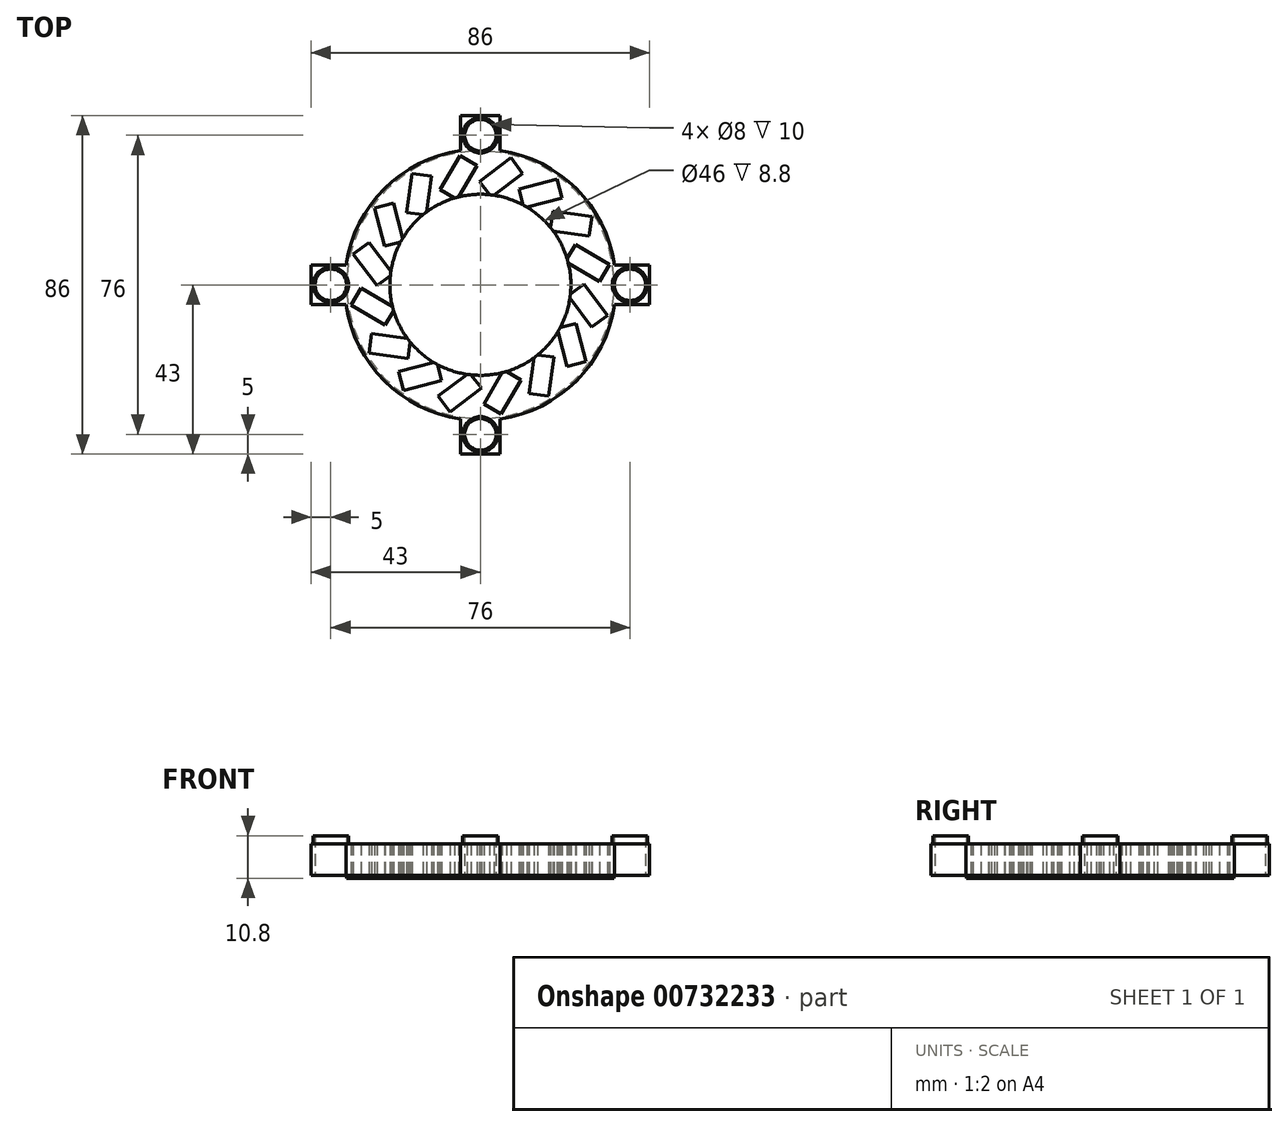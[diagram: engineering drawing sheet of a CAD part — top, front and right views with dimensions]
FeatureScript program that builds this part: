
annotation { "Feature Type Name" : "Feature", "Feature Type Description" : "" }
export const myFeature = defineFeature(function(context is Context, id is Id, definition is map)
    precondition{}
    {
        {
            var Q0;
            Q0=qCreatedBy(makeId("Top.planeOp"),FACE);
            var sketch = newSketch(context, id + "F0", { "sketchPlane" : qUnion([Q0])});
            skCircle(sketch, "E0", {"center": v(0, 0) * mm, "radius": 23 * mm});
            skCircle(sketch, "E1", {"center": v(0, 0) * mm, "radius": 34 * mm});
            skLineSegment(sketch, "E2", {"start": v(0, 0) * mm, "end": v(1.57, 29.96) * mm, "construction": true});
            skLineSegment(sketch, "E3.bottom", {"start": v(9.26, 30.29) * mm, "end": v(10.76, 28.3) * mm});
            skLineSegment(sketch, "E3.top", {"start": v(1.27, 24.27) * mm, "end": v(2.78, 22.27) * mm});
            skLineSegment(sketch, "E3.right", {"start": v(10.76, 28.3) * mm, "end": v(2.78, 22.27) * mm});
            skLineSegment(sketch, "E4.MirrorCS", {"start": v(7.75, 32.28) * mm, "end": v(-0.23, 26.27) * mm});
            skLineSegment(sketch, "E5.MirrorCS", {"start": v(1.27, 24.27) * mm, "end": v(-0.23, 26.27) * mm});
            skLineSegment(sketch, "E6.MirrorCS", {"start": v(9.26, 30.29) * mm, "end": v(7.75, 32.28) * mm});
            skLineSegment(sketch, "E7", {"start": v(0, 0) * mm, "end": v(35, 0) * mm, "construction": true});
            skPoint(sketch, "E8", {"position": v(1.2, 22.97) * mm});
            skCircle(sketch, "E9", {"center": v(0, 0) * mm, "radius": 38 * mm});
            skCircle(sketch, "E10", {"center": v(0, 0) * mm, "radius": 40 * mm});
            skLineSegment(sketch, "E11.1.0", {"start": v(-5.2, 32.8) * mm, "end": v(-10.27, 24.18) * mm});
            skLineSegment(sketch, "E11.1.1", {"start": v(-3.04, 31.52) * mm, "end": v(-5.2, 32.8) * mm});
            skLineSegment(sketch, "E11.1.2", {"start": v(-3.04, 31.52) * mm, "end": v(-0.88, 30.26) * mm});
            skLineSegment(sketch, "E11.1.3", {"start": v(-0.88, 30.26) * mm, "end": v(-5.96, 21.64) * mm});
            skLineSegment(sketch, "E11.1.4", {"start": v(-8.11, 22.9) * mm, "end": v(-5.96, 21.64) * mm});
            skLineSegment(sketch, "E11.1.5", {"start": v(-8.11, 22.9) * mm, "end": v(-10.27, 24.18) * mm});
            skLineSegment(sketch, "E11.2.0", {"start": v(-17.35, 28.31) * mm, "end": v(-18.74, 18.4) * mm});
            skLineSegment(sketch, "E11.2.1", {"start": v(-14.87, 27.96) * mm, "end": v(-17.35, 28.31) * mm});
            skLineSegment(sketch, "E11.2.2", {"start": v(-14.87, 27.96) * mm, "end": v(-12.4, 27.61) * mm});
            skLineSegment(sketch, "E11.2.3", {"start": v(-12.4, 27.61) * mm, "end": v(-13.79, 17.71) * mm});
            skLineSegment(sketch, "E11.2.4", {"start": v(-16.26, 18.06) * mm, "end": v(-13.79, 17.71) * mm});
            skLineSegment(sketch, "E11.2.5", {"start": v(-16.26, 18.06) * mm, "end": v(-18.74, 18.4) * mm});
            skLineSegment(sketch, "E11.3.0", {"start": v(-26.86, 19.52) * mm, "end": v(-24.35, 9.84) * mm});
            skLineSegment(sketch, "E11.3.1", {"start": v(-24.44, 20.14) * mm, "end": v(-26.86, 19.52) * mm});
            skLineSegment(sketch, "E11.3.2", {"start": v(-24.44, 20.14) * mm, "end": v(-22.02, 20.77) * mm});
            skLineSegment(sketch, "E11.3.3", {"start": v(-22.02, 20.77) * mm, "end": v(-19.51, 11.09) * mm});
            skLineSegment(sketch, "E11.3.4", {"start": v(-21.93, 10.46) * mm, "end": v(-19.51, 11.09) * mm});
            skLineSegment(sketch, "E11.3.5", {"start": v(-21.93, 10.46) * mm, "end": v(-24.35, 9.84) * mm});
            skLineSegment(sketch, "E11.4.0", {"start": v(-32.28, 7.75) * mm, "end": v(-26.27, -0.23) * mm});
            skLineSegment(sketch, "E11.4.1", {"start": v(-30.29, 9.26) * mm, "end": v(-32.28, 7.75) * mm});
            skLineSegment(sketch, "E11.4.2", {"start": v(-30.29, 9.26) * mm, "end": v(-28.3, 10.76) * mm});
            skLineSegment(sketch, "E11.4.3", {"start": v(-28.3, 10.76) * mm, "end": v(-22.27, 2.78) * mm});
            skLineSegment(sketch, "E11.4.4", {"start": v(-24.27, 1.27) * mm, "end": v(-22.27, 2.78) * mm});
            skLineSegment(sketch, "E11.4.5", {"start": v(-24.27, 1.27) * mm, "end": v(-26.27, -0.23) * mm});
            skLineSegment(sketch, "E11.5.0", {"start": v(-32.8, -5.2) * mm, "end": v(-24.18, -10.27) * mm});
            skLineSegment(sketch, "E11.5.1", {"start": v(-31.52, -3.04) * mm, "end": v(-32.8, -5.2) * mm});
            skLineSegment(sketch, "E11.5.2", {"start": v(-31.52, -3.04) * mm, "end": v(-30.26, -0.88) * mm});
            skLineSegment(sketch, "E11.5.3", {"start": v(-30.26, -0.88) * mm, "end": v(-21.64, -5.96) * mm});
            skLineSegment(sketch, "E11.5.4", {"start": v(-22.9, -8.11) * mm, "end": v(-21.64, -5.96) * mm});
            skLineSegment(sketch, "E11.5.5", {"start": v(-22.9, -8.11) * mm, "end": v(-24.18, -10.27) * mm});
            skLineSegment(sketch, "E11.6.0", {"start": v(-28.31, -17.35) * mm, "end": v(-18.4, -18.74) * mm});
            skLineSegment(sketch, "E11.6.1", {"start": v(-27.96, -14.87) * mm, "end": v(-28.31, -17.35) * mm});
            skLineSegment(sketch, "E11.6.2", {"start": v(-27.96, -14.87) * mm, "end": v(-27.61, -12.4) * mm});
            skLineSegment(sketch, "E11.6.3", {"start": v(-27.61, -12.4) * mm, "end": v(-17.71, -13.79) * mm});
            skLineSegment(sketch, "E11.6.4", {"start": v(-18.06, -16.26) * mm, "end": v(-17.71, -13.79) * mm});
            skLineSegment(sketch, "E11.6.5", {"start": v(-18.06, -16.26) * mm, "end": v(-18.4, -18.74) * mm});
            skLineSegment(sketch, "E11.7.0", {"start": v(-19.52, -26.86) * mm, "end": v(-9.84, -24.35) * mm});
            skLineSegment(sketch, "E11.7.1", {"start": v(-20.14, -24.44) * mm, "end": v(-19.52, -26.86) * mm});
            skLineSegment(sketch, "E11.7.2", {"start": v(-20.14, -24.44) * mm, "end": v(-20.77, -22.02) * mm});
            skLineSegment(sketch, "E11.7.3", {"start": v(-20.77, -22.02) * mm, "end": v(-11.09, -19.51) * mm});
            skLineSegment(sketch, "E11.7.4", {"start": v(-10.46, -21.93) * mm, "end": v(-11.09, -19.51) * mm});
            skLineSegment(sketch, "E11.7.5", {"start": v(-10.46, -21.93) * mm, "end": v(-9.84, -24.35) * mm});
            skLineSegment(sketch, "E11.8.0", {"start": v(-7.75, -32.28) * mm, "end": v(0.23, -26.27) * mm});
            skLineSegment(sketch, "E11.8.1", {"start": v(-9.26, -30.29) * mm, "end": v(-7.75, -32.28) * mm});
            skLineSegment(sketch, "E11.8.2", {"start": v(-9.26, -30.29) * mm, "end": v(-10.76, -28.3) * mm});
            skLineSegment(sketch, "E11.8.3", {"start": v(-10.76, -28.3) * mm, "end": v(-2.78, -22.27) * mm});
            skLineSegment(sketch, "E11.8.4", {"start": v(-1.27, -24.27) * mm, "end": v(-2.78, -22.27) * mm});
            skLineSegment(sketch, "E11.8.5", {"start": v(-1.27, -24.27) * mm, "end": v(0.23, -26.27) * mm});
            skLineSegment(sketch, "E11.9.0", {"start": v(5.2, -32.8) * mm, "end": v(10.27, -24.18) * mm});
            skLineSegment(sketch, "E11.9.1", {"start": v(3.04, -31.52) * mm, "end": v(5.2, -32.8) * mm});
            skLineSegment(sketch, "E11.9.2", {"start": v(3.04, -31.52) * mm, "end": v(0.88, -30.26) * mm});
            skLineSegment(sketch, "E11.9.3", {"start": v(0.88, -30.26) * mm, "end": v(5.96, -21.64) * mm});
            skLineSegment(sketch, "E11.9.4", {"start": v(8.11, -22.9) * mm, "end": v(5.96, -21.64) * mm});
            skLineSegment(sketch, "E11.9.5", {"start": v(8.11, -22.9) * mm, "end": v(10.27, -24.18) * mm});
            skLineSegment(sketch, "E11.10.0", {"start": v(17.35, -28.31) * mm, "end": v(18.74, -18.4) * mm});
            skLineSegment(sketch, "E11.10.1", {"start": v(14.87, -27.96) * mm, "end": v(17.35, -28.31) * mm});
            skLineSegment(sketch, "E11.10.2", {"start": v(14.87, -27.96) * mm, "end": v(12.4, -27.61) * mm});
            skLineSegment(sketch, "E11.10.3", {"start": v(12.4, -27.61) * mm, "end": v(13.79, -17.71) * mm});
            skLineSegment(sketch, "E11.10.4", {"start": v(16.26, -18.06) * mm, "end": v(13.79, -17.71) * mm});
            skLineSegment(sketch, "E11.10.5", {"start": v(16.26, -18.06) * mm, "end": v(18.74, -18.4) * mm});
            skLineSegment(sketch, "E11.11.0", {"start": v(26.86, -19.52) * mm, "end": v(24.35, -9.84) * mm});
            skLineSegment(sketch, "E11.11.1", {"start": v(24.44, -20.14) * mm, "end": v(26.86, -19.52) * mm});
            skLineSegment(sketch, "E11.11.2", {"start": v(24.44, -20.14) * mm, "end": v(22.02, -20.77) * mm});
            skLineSegment(sketch, "E11.11.3", {"start": v(22.02, -20.77) * mm, "end": v(19.51, -11.09) * mm});
            skLineSegment(sketch, "E11.11.4", {"start": v(21.93, -10.46) * mm, "end": v(19.51, -11.09) * mm});
            skLineSegment(sketch, "E11.11.5", {"start": v(21.93, -10.46) * mm, "end": v(24.35, -9.84) * mm});
            skLineSegment(sketch, "E11.12.0", {"start": v(32.28, -7.75) * mm, "end": v(26.27, 0.23) * mm});
            skLineSegment(sketch, "E11.12.1", {"start": v(30.29, -9.26) * mm, "end": v(32.28, -7.75) * mm});
            skLineSegment(sketch, "E11.12.2", {"start": v(30.29, -9.26) * mm, "end": v(28.3, -10.76) * mm});
            skLineSegment(sketch, "E11.12.3", {"start": v(28.3, -10.76) * mm, "end": v(22.27, -2.78) * mm});
            skLineSegment(sketch, "E11.12.4", {"start": v(24.27, -1.27) * mm, "end": v(22.27, -2.78) * mm});
            skLineSegment(sketch, "E11.12.5", {"start": v(24.27, -1.27) * mm, "end": v(26.27, 0.23) * mm});
            skLineSegment(sketch, "E11.13.0", {"start": v(32.8, 5.2) * mm, "end": v(24.18, 10.27) * mm});
            skLineSegment(sketch, "E11.13.1", {"start": v(31.52, 3.04) * mm, "end": v(32.8, 5.2) * mm});
            skLineSegment(sketch, "E11.13.2", {"start": v(31.52, 3.04) * mm, "end": v(30.26, 0.88) * mm});
            skLineSegment(sketch, "E11.13.3", {"start": v(30.26, 0.88) * mm, "end": v(21.64, 5.96) * mm});
            skLineSegment(sketch, "E11.13.4", {"start": v(22.9, 8.11) * mm, "end": v(21.64, 5.96) * mm});
            skLineSegment(sketch, "E11.13.5", {"start": v(22.9, 8.11) * mm, "end": v(24.18, 10.27) * mm});
            skLineSegment(sketch, "E11.14.0", {"start": v(28.31, 17.35) * mm, "end": v(18.4, 18.74) * mm});
            skLineSegment(sketch, "E11.14.1", {"start": v(27.96, 14.87) * mm, "end": v(28.31, 17.35) * mm});
            skLineSegment(sketch, "E11.14.2", {"start": v(27.96, 14.87) * mm, "end": v(27.61, 12.4) * mm});
            skLineSegment(sketch, "E11.14.3", {"start": v(27.61, 12.4) * mm, "end": v(17.71, 13.79) * mm});
            skLineSegment(sketch, "E11.14.4", {"start": v(18.06, 16.26) * mm, "end": v(17.71, 13.79) * mm});
            skLineSegment(sketch, "E11.14.5", {"start": v(18.06, 16.26) * mm, "end": v(18.4, 18.74) * mm});
            skLineSegment(sketch, "E11.15.0", {"start": v(19.52, 26.86) * mm, "end": v(9.84, 24.35) * mm});
            skLineSegment(sketch, "E11.15.1", {"start": v(20.14, 24.44) * mm, "end": v(19.52, 26.86) * mm});
            skLineSegment(sketch, "E11.15.2", {"start": v(20.14, 24.44) * mm, "end": v(20.77, 22.02) * mm});
            skLineSegment(sketch, "E11.15.3", {"start": v(20.77, 22.02) * mm, "end": v(11.09, 19.51) * mm});
            skLineSegment(sketch, "E11.15.4", {"start": v(10.46, 21.93) * mm, "end": v(11.09, 19.51) * mm});
            skLineSegment(sketch, "E11.15.5", {"start": v(10.46, 21.93) * mm, "end": v(9.84, 24.35) * mm});
            skSolve(sketch);
        }
        {
            var Q0;
            Q0=qCreatedBy(makeId("Top.planeOp"),FACE);
            var sketch = newSketch(context, id + "F1", { "sketchPlane" : qUnion([Q0])});
            skArc(sketch, "E12", {"start": v(-34.4, -2.7) * mm, "mid": v(-24.4, -24.4) * mm, "end": v(-2.7, -34.4) * mm});
            skCircle(sketch, "E13", {"center": v(0, 0) * mm, "radius": 23 * mm});
            skArc(sketch, "E14", {"start": v(-33.94, -1.95) * mm, "mid": v(-24.04, -24.04) * mm, "end": v(-1.95, -33.94) * mm});
            skLineSegment(sketch, "E15", {"start": v(0, 0) * mm, "end": v(34, 0) * mm, "construction": true});
            skCircle(sketch, "E16", {"center": v(0, 38) * mm, "radius": 4 * mm});
            skCircle(sketch, "E17", {"center": v(0, 38) * mm, "radius": 4.5 * mm});
            skLineSegment(sketch, "E18", {"start": v(0, 42.5) * mm, "end": v(0, 43) * mm});
            skLineSegment(sketch, "E19", {"start": v(0, 43) * mm, "end": v(5, 43) * mm});
            skLineSegment(sketch, "E20", {"start": v(5, 43) * mm, "end": v(5, 34.14) * mm});
            skLineSegment(sketch, "E21.MirrorCS", {"start": v(0, 43) * mm, "end": v(-5, 43) * mm});
            skLineSegment(sketch, "E22.MirrorCS", {"start": v(-5, 43) * mm, "end": v(-5, 34.14) * mm});
            skLineSegment(sketch, "E23.1.0", {"start": v(-43, 0) * mm, "end": v(-43, 5) * mm});
            skLineSegment(sketch, "E23.1.1", {"start": v(-43, 5) * mm, "end": v(-34.14, 5) * mm});
            skLineSegment(sketch, "E23.1.2", {"start": v(-43, 0) * mm, "end": v(-43, -5) * mm});
            skLineSegment(sketch, "E23.1.3", {"start": v(-43, -5) * mm, "end": v(-34.14, -5) * mm});
            skCircle(sketch, "E23.1.4", {"center": v(-38, 0) * mm, "radius": 4.5 * mm});
            skCircle(sketch, "E23.1.5", {"center": v(-38, 0) * mm, "radius": 4 * mm});
            skLineSegment(sketch, "E23.2.0", {"start": v(0, -43) * mm, "end": v(-5, -43) * mm});
            skLineSegment(sketch, "E23.2.1", {"start": v(-5, -43) * mm, "end": v(-5, -34.14) * mm});
            skLineSegment(sketch, "E23.2.2", {"start": v(0, -43) * mm, "end": v(5, -43) * mm});
            skLineSegment(sketch, "E23.2.3", {"start": v(5, -43) * mm, "end": v(5, -34.14) * mm});
            skCircle(sketch, "E23.2.4", {"center": v(0, -38) * mm, "radius": 4.5 * mm});
            skCircle(sketch, "E23.2.5", {"center": v(0, -38) * mm, "radius": 4 * mm});
            skLineSegment(sketch, "E23.3.0", {"start": v(43, 0) * mm, "end": v(43, -5) * mm});
            skLineSegment(sketch, "E23.3.1", {"start": v(43, -5) * mm, "end": v(34.14, -5) * mm});
            skLineSegment(sketch, "E23.3.2", {"start": v(43, 0) * mm, "end": v(43, 5) * mm});
            skLineSegment(sketch, "E23.3.3", {"start": v(43, 5) * mm, "end": v(34.14, 5) * mm});
            skCircle(sketch, "E23.3.4", {"center": v(38, 0) * mm, "radius": 4.5 * mm});
            skCircle(sketch, "E23.3.5", {"center": v(38, 0) * mm, "radius": 4 * mm});
            skArc(sketch, "E24.trimOffspring", {"start": v(33.94, 1.95) * mm, "mid": v(24.04, 24.04) * mm, "end": v(1.95, 33.94) * mm});
            skArc(sketch, "E25.trimOffspring", {"start": v(34.4, 2.7) * mm, "mid": v(24.4, 24.4) * mm, "end": v(2.7, 34.4) * mm});
            skArc(sketch, "E26.trimOffspring", {"start": v(-2.7, 34.4) * mm, "mid": v(-24.4, 24.4) * mm, "end": v(-34.4, 2.7) * mm});
            skArc(sketch, "E27.trimOffspring", {"start": v(2.7, -34.4) * mm, "mid": v(24.4, -24.4) * mm, "end": v(34.4, -2.7) * mm});
            skArc(sketch, "E28.trimOffspring", {"start": v(1.95, -33.94) * mm, "mid": v(24.04, -24.04) * mm, "end": v(33.94, -1.95) * mm});
            skArc(sketch, "E29.trimOffspring", {"start": v(-1.95, 33.94) * mm, "mid": v(-24.04, 24.04) * mm, "end": v(-33.94, 1.95) * mm});
            skSolve(sketch);
        }
        {
            var Q0;
            Q0=qSketchRegion(id+"F1",true);
            var Q1;
            Q1=makeQuery(id+"F1.imprint","IMPRINT",FACE,{"disambiguationData":[TD([[makeQuery(id+"F1.imprint","IMPRINT",EDGE,{"derivedFrom":sQuery(id+"F1.wireOp",EDGE,"d15ed5a5-fd29-49d6-a964-e686c6378fca.3.5")}),1.0]])]});
            var Q2;
            Q2=makeQuery(id+"F1.imprint","IMPRINT",FACE,{"disambiguationData":[TD([[makeQuery(id+"F1.imprint","IMPRINT",EDGE,{"derivedFrom":sQuery(id+"F1.wireOp",EDGE,"d15ed5a5-fd29-49d6-a964-e686c6378fca.3.4")}),1.0]])]});
            var Q3;
            Q3=makeQuery(id+"F1.imprint","IMPRINT",FACE,{"disambiguationData":[TD([[makeQuery(id+"F1.imprint","IMPRINT",EDGE,{"derivedFrom":sQuery(id+"F1.wireOp",EDGE,"nMKEX2UH-BGaZ-hXa7-XY8u-qAvmxy0yM5Br")}),1.0]])]});
            var Q4;
            Q4=makeQuery(id+"F1.imprint","IMPRINT",FACE,{"disambiguationData":[TD([[makeQuery(id+"F1.imprint","IMPRINT",EDGE,{"derivedFrom":sQuery(id+"F1.wireOp",EDGE,"nMKEX2UH-BGaZ-hXa7-XY8u-qAvmxy0yM5Br")}),-1.0]])]});
            var Q5;
            Q5=makeQuery(id+"F1.imprint","IMPRINT",FACE,{"disambiguationData":[TD([[makeQuery(id+"F1.imprint","IMPRINT",EDGE,{"derivedFrom":sQuery(id+"F1.wireOp",EDGE,"d15ed5a5-fd29-49d6-a964-e686c6378fca.1.5")}),1.0]])]});
            var Q6;
            Q6=makeQuery(id+"F1.imprint","IMPRINT",FACE,{"disambiguationData":[TD([[makeQuery(id+"F1.imprint","IMPRINT",EDGE,{"derivedFrom":sQuery(id+"F1.wireOp",EDGE,"d15ed5a5-fd29-49d6-a964-e686c6378fca.1.4")}),1.0]])]});
            var Q7;
            Q7=makeQuery(id+"F1.imprint","IMPRINT",FACE,{"disambiguationData":[TD([[makeQuery(id+"F1.imprint","IMPRINT",EDGE,{"derivedFrom":sQuery(id+"F1.wireOp",EDGE,"d15ed5a5-fd29-49d6-a964-e686c6378fca.2.5")}),1.0]])]});
            var Q8;
            Q8=makeQuery(id+"F1.imprint","IMPRINT",FACE,{"disambiguationData":[TD([[makeQuery(id+"F1.imprint","IMPRINT",EDGE,{"derivedFrom":sQuery(id+"F1.wireOp",EDGE,"d15ed5a5-fd29-49d6-a964-e686c6378fca.2.4")}),1.0]])]});
            var Q9;
            {var subQ98=sQuery(id+"F1.wireOp",EDGE,"f3e762ff-506c-4368-bb15-f758a9c07f8b.bottom");Q9=makeQuery(id+"F1.imprint","IMPRINT",FACE,{"disambiguationData":[TD([[makeQuery(id+"F1.imprint","IMPRINT",EDGE,{"derivedFrom":subQ98}),1.0]])]});}
            var Q10;
            {var subQ16=sQuery(id+"F1.wireOp",EDGE,"E14");Q10=makeQuery(id+"F1.imprint","IMPRINT",FACE,{"disambiguationData":[TD([[makeQuery(id+"F1.imprint","IMPRINT",EDGE,{"derivedFrom":subQ16}),1.0]])]});}
            extrude(context, id + "F2", {"entities" : qUnion([Q0, Q1, Q2, Q3, Q4, Q5, Q6, Q7, Q8, Q9, Q10]), "depth" : 8 * mm, "offsetDistance" : 25 * mm});
        }
        {
            var Q0;
            Q0=makeQuery(id+"F1.imprint","IMPRINT",FACE,{"disambiguationData":[TD([[makeQuery(id+"F1.imprint","IMPRINT",EDGE,{"derivedFrom":sQuery(id+"F1.wireOp",EDGE,"E23.3.5")}),-1.0]])]});
            var Q1;
            Q1=makeQuery(id+"F1.imprint","IMPRINT",FACE,{"disambiguationData":[TD([[makeQuery(id+"F1.imprint","IMPRINT",EDGE,{"derivedFrom":sQuery(id+"F1.wireOp",EDGE,"E23.2.5")}),-1.0]])]});
            var Q2;
            Q2=makeQuery(id+"F1.imprint","IMPRINT",FACE,{"disambiguationData":[TD([[makeQuery(id+"F1.imprint","IMPRINT",EDGE,{"derivedFrom":sQuery(id+"F1.wireOp",EDGE,"E23.1.5")}),-1.0]])]});
            var Q3;
            Q3=makeQuery(id+"F1.imprint","IMPRINT",FACE,{"disambiguationData":[TD([[makeQuery(id+"F1.imprint","IMPRINT",EDGE,{"derivedFrom":sQuery(id+"F1.wireOp",EDGE,"E16")}),-1.0]])]});
            extrude(context, id + "F3", {"entities" : qUnion([Q0, Q1, Q2, Q3]), "operationType" : NewBodyOperationType.ADD, "depth" : 10 * mm, "offsetDistance" : 25 * mm});
        }
        {
            var Q0;
            Q0=makeQuery(id+"F1.imprint","IMPRINT",FACE,{"disambiguationData":[TD([[makeQuery(id+"F1.imprint","IMPRINT",EDGE,{"derivedFrom":sQuery(id+"F1.wireOp",EDGE,"E13")}),-1.0]])]});
            extrude(context, id + "F4", {"entities" : qUnion([Q0]), "operationType" : NewBodyOperationType.ADD, "oppositeDirection" : true, "depth" : 0.8 * mm, "offsetDistance" : 25 * mm});
        }
        {
            var Q0;
            Q0=makeQuery(id+"F0.imprint","IMPRINT",FACE,{"disambiguationData":[TD([[makeQuery(id+"F0.imprint","IMPRINT",EDGE,{"derivedFrom":sQuery(id+"F0.wireOp",EDGE,"E11.2.0")}),1.0]])]});
            var Q1;
            Q1=makeQuery(id+"F0.imprint","IMPRINT",FACE,{"disambiguationData":[TD([[makeQuery(id+"F0.imprint","IMPRINT",EDGE,{"derivedFrom":sQuery(id+"F0.wireOp",EDGE,"E11.1.0")}),1.0]])]});
            var Q2;
            {var subQ4=sQuery(id+"F0.wireOp",EDGE,"E3.bottom");Q2=makeQuery(id+"F0.imprint","IMPRINT",FACE,{"disambiguationData":[TD([[makeQuery(id+"F0.imprint","IMPRINT",EDGE,{"derivedFrom":subQ4}),-1.0]])]});}
            var Q3;
            Q3=makeQuery(id+"F0.imprint","IMPRINT",FACE,{"disambiguationData":[TD([[makeQuery(id+"F0.imprint","IMPRINT",EDGE,{"derivedFrom":sQuery(id+"F0.wireOp",EDGE,"E11.15.0")}),1.0]])]});
            var Q4;
            Q4=makeQuery(id+"F0.imprint","IMPRINT",FACE,{"disambiguationData":[TD([[makeQuery(id+"F0.imprint","IMPRINT",EDGE,{"derivedFrom":sQuery(id+"F0.wireOp",EDGE,"E11.14.0")}),1.0]])]});
            var Q5;
            Q5=makeQuery(id+"F0.imprint","IMPRINT",FACE,{"disambiguationData":[TD([[makeQuery(id+"F0.imprint","IMPRINT",EDGE,{"derivedFrom":sQuery(id+"F0.wireOp",EDGE,"E11.13.0")}),1.0]])]});
            var Q6;
            Q6=makeQuery(id+"F0.imprint","IMPRINT",FACE,{"disambiguationData":[TD([[makeQuery(id+"F0.imprint","IMPRINT",EDGE,{"derivedFrom":sQuery(id+"F0.wireOp",EDGE,"E11.12.0")}),1.0]])]});
            var Q7;
            Q7=makeQuery(id+"F0.imprint","IMPRINT",FACE,{"disambiguationData":[TD([[makeQuery(id+"F0.imprint","IMPRINT",EDGE,{"derivedFrom":sQuery(id+"F0.wireOp",EDGE,"E11.11.0")}),1.0]])]});
            var Q8;
            Q8=makeQuery(id+"F0.imprint","IMPRINT",FACE,{"disambiguationData":[TD([[makeQuery(id+"F0.imprint","IMPRINT",EDGE,{"derivedFrom":sQuery(id+"F0.wireOp",EDGE,"E11.10.0")}),1.0]])]});
            var Q9;
            Q9=makeQuery(id+"F0.imprint","IMPRINT",FACE,{"disambiguationData":[TD([[makeQuery(id+"F0.imprint","IMPRINT",EDGE,{"derivedFrom":sQuery(id+"F0.wireOp",EDGE,"E11.9.0")}),1.0]])]});
            var Q10;
            Q10=makeQuery(id+"F0.imprint","IMPRINT",FACE,{"disambiguationData":[TD([[makeQuery(id+"F0.imprint","IMPRINT",EDGE,{"derivedFrom":sQuery(id+"F0.wireOp",EDGE,"E11.8.0")}),1.0]])]});
            var Q11;
            Q11=makeQuery(id+"F0.imprint","IMPRINT",FACE,{"disambiguationData":[TD([[makeQuery(id+"F0.imprint","IMPRINT",EDGE,{"derivedFrom":sQuery(id+"F0.wireOp",EDGE,"E11.7.0")}),1.0]])]});
            var Q12;
            Q12=makeQuery(id+"F0.imprint","IMPRINT",FACE,{"disambiguationData":[TD([[makeQuery(id+"F0.imprint","IMPRINT",EDGE,{"derivedFrom":sQuery(id+"F0.wireOp",EDGE,"E11.6.0")}),1.0]])]});
            var Q13;
            Q13=makeQuery(id+"F0.imprint","IMPRINT",FACE,{"disambiguationData":[TD([[makeQuery(id+"F0.imprint","IMPRINT",EDGE,{"derivedFrom":sQuery(id+"F0.wireOp",EDGE,"E11.5.0")}),1.0]])]});
            var Q14;
            Q14=makeQuery(id+"F0.imprint","IMPRINT",FACE,{"disambiguationData":[TD([[makeQuery(id+"F0.imprint","IMPRINT",EDGE,{"derivedFrom":sQuery(id+"F0.wireOp",EDGE,"E11.4.0")}),1.0]])]});
            var Q15;
            Q15=makeQuery(id+"F0.imprint","IMPRINT",FACE,{"disambiguationData":[TD([[makeQuery(id+"F0.imprint","IMPRINT",EDGE,{"derivedFrom":sQuery(id+"F0.wireOp",EDGE,"E11.3.0")}),1.0]])]});
            extrude(context, id + "F5", {"entities" : qUnion([Q0, Q1, Q2, Q3, Q4, Q5, Q6, Q7, Q8, Q9, Q10, Q11, Q12, Q13, Q14, Q15]), "operationType" : NewBodyOperationType.REMOVE, "depth" : 25 * mm, "offsetDistance" : 25 * mm});
        }
    });
